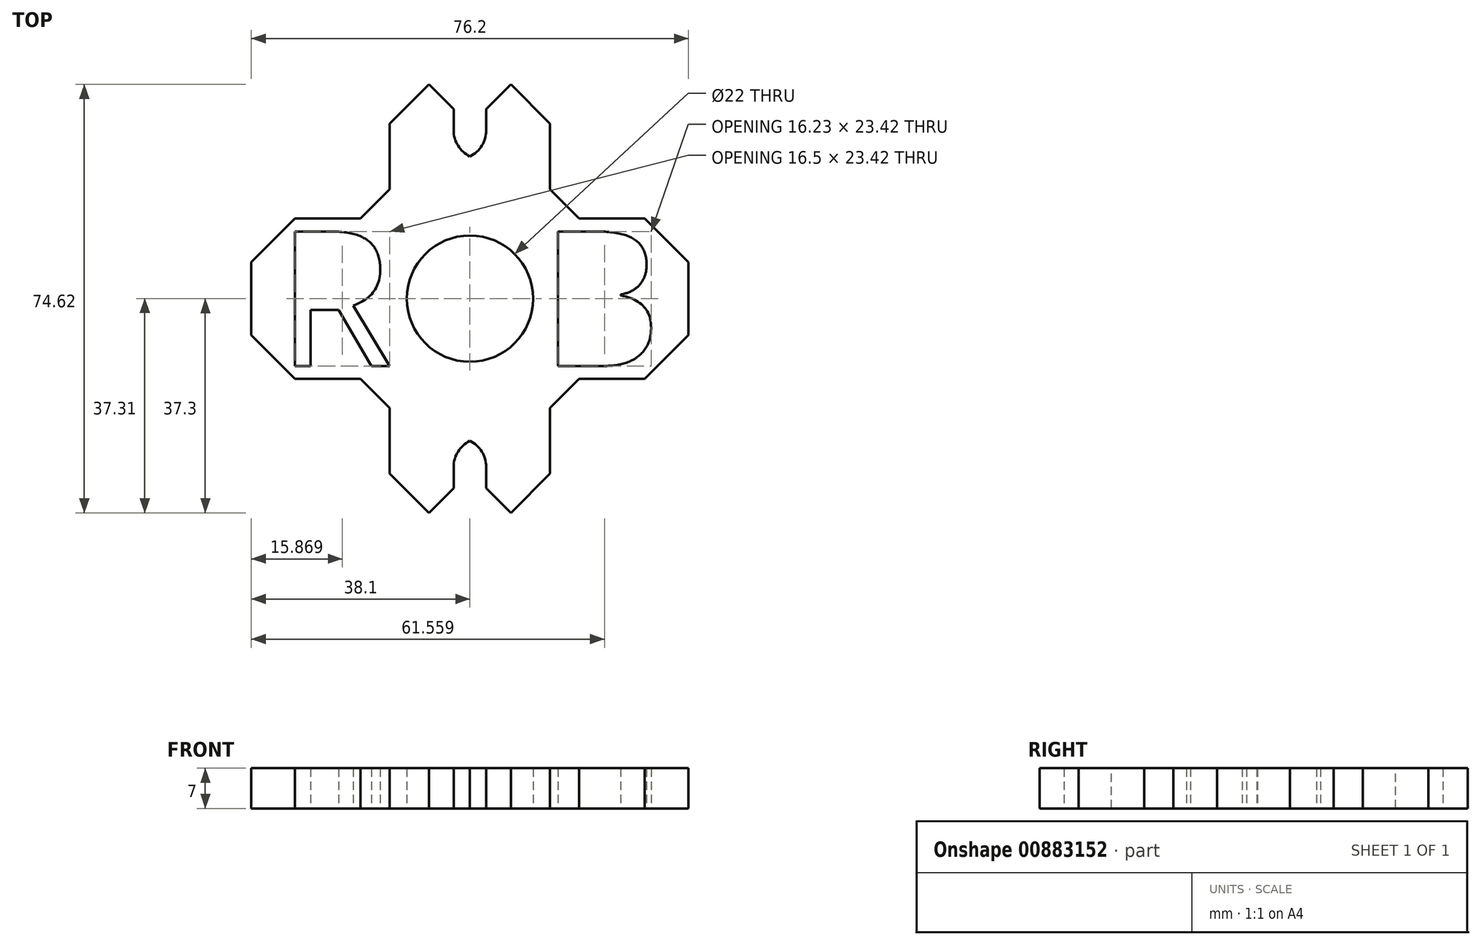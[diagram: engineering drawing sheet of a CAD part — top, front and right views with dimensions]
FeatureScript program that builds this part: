
annotation { "Feature Type Name" : "Feature", "Feature Type Description" : "" }
export const myFeature = defineFeature(function(context is Context, id is Id, definition is map)
    precondition{}
    {
        {
            var Q0;
            Q0=qCreatedBy(makeId("Top.planeOp"),FACE);
            var sketch = newSketch(context, id + "F0", { "sketchPlane" : qUnion([Q0])});
            skCircle(sketch, "E0", {"center": v(0, 0) * mm, "radius": 11 * mm});
            skLineSegment(sketch, "E1.bottom", {"start": v(-38.1, -13.97) * mm, "end": v(38.1, -13.97) * mm});
            skLineSegment(sketch, "E1.top", {"start": v(-38.1, 13.97) * mm, "end": v(38.1, 13.97) * mm});
            skLineSegment(sketch, "E1.left", {"start": v(-38.1, -13.97) * mm, "end": v(-38.1, 13.97) * mm});
            skLineSegment(sketch, "E1.right", {"start": v(38.1, -13.97) * mm, "end": v(38.1, 13.97) * mm});
            skText(sketch, "E2", { "text": "ROB", "fontName": "OpenSans-Regular.ttf"});
            skLineSegment(sketch, "E3.bottom", {"start": v(-13.97, -38.1) * mm, "end": v(13.97, -38.1) * mm});
            skLineSegment(sketch, "E3.top", {"start": v(-13.97, 38.1) * mm, "end": v(13.97, 38.1) * mm});
            skLineSegment(sketch, "E3.left", {"start": v(-13.97, -38.1) * mm, "end": v(-13.97, 38.1) * mm});
            skLineSegment(sketch, "E3.right", {"start": v(13.97, -38.1) * mm, "end": v(13.97, 38.1) * mm});
            const initialGuessF0  = {"E2": [-0.0337, -0.01172, 1, 0, 0.02362]};
            skSetInitialGuess(sketch, initialGuessF0);
            skSolve(sketch);
        }
        {
            var Q0;
            Q0=makeQuery(id+"F0.imprint","IMPRINT",FACE,{"disambiguationData":[TD([[makeQuery(id+"F0.imprint","IMPRINT",EDGE,{"derivedFrom":sQuery(id+"F0.wireOp",EDGE,"E1.bottom")}),1.0]])]});
            var Q1;
            {var subQ0=sQuery(id+"F0.wireOp",EDGE,"E2.sketch_text.stroke-19");Q1=makeQuery(id+"F0.imprint","IMPRINT",FACE,{"disambiguationData":[TD([[makeQuery(id+"F0.imprint","IMPRINT",EDGE,{"derivedFrom":subQ0}),-1.0]])]});}
            extrude(context, id + "F1", {"entities" : qUnion([Q0, Q1]), "depth" : 7 * mm, "offsetDistance" : 25.4 * mm});
        }
        {
            var Q0;
            {var subQ0=sQuery(id+"F0.wireOp",EDGE,"E1.left");Q0=makeQuery(id+"F0.imprint","IMPRINT",FACE,{"disambiguationData":[TD([[makeQuery(id+"F0.imprint","IMPRINT",EDGE,{"derivedFrom":subQ0}),-1.0]])]});}
            var Q1;
            {var subQ6=sQuery(id+"F0.wireOp",EDGE,"E2.sketch_text.stroke-19");Q1=makeQuery(id+"F0.imprint","IMPRINT",FACE,{"disambiguationData":[TD([[makeQuery(id+"F0.imprint","IMPRINT",EDGE,{"derivedFrom":subQ6}),1.0]])]});}
            var Q2;
            {var subQ0=sQuery(id+"F0.wireOp",EDGE,"E2.sketch_text.stroke-19");Q2=makeQuery(id+"F0.imprint","IMPRINT",FACE,{"disambiguationData":[TD([[makeQuery(id+"F0.imprint","IMPRINT",EDGE,{"derivedFrom":subQ0}),-1.0]])]});}
            var Q3;
            {var subQ0=sQuery(id+"F0.wireOp",EDGE,"E1.right");Q3=makeQuery(id+"F0.imprint","IMPRINT",FACE,{"disambiguationData":[TD([[makeQuery(id+"F0.imprint","IMPRINT",EDGE,{"derivedFrom":subQ0}),1.0]])]});}
            var Q4;
            {var subQ5=sQuery(id+"F0.wireOp",EDGE,"E3.top");Q4=makeQuery(id+"F0.imprint","IMPRINT",FACE,{"disambiguationData":[TD([[makeQuery(id+"F0.imprint","IMPRINT",EDGE,{"derivedFrom":subQ5}),-1.0]])]});}
            var Q5;
            {var subQ5=sQuery(id+"F0.wireOp",EDGE,"E3.bottom");Q5=makeQuery(id+"F0.imprint","IMPRINT",FACE,{"disambiguationData":[TD([[makeQuery(id+"F0.imprint","IMPRINT",EDGE,{"derivedFrom":subQ5}),1.0]])]});}
            extrude(context, id + "F2", {"entities" : qUnion([Q0, Q1, Q2, Q3, Q4, Q5]), "operationType" : NewBodyOperationType.ADD, "depth" : 7 * mm, "offsetDistance" : 25.4 * mm});
        }
        {
            var Q0;
            Q0=makeQuery(id+"F2.opExtrude","SWEPT_EDGE",EDGE,{"disambiguationData":[OSD([sQuery(id+"F0.wireOp",EDGE,"E3.top"),sQuery(id+"F0.wireOp",EDGE,"E3.right")])]});
            var Q1;
            Q1=makeQuery(id+"F2.opExtrude","SWEPT_EDGE",EDGE,{"disambiguationData":[OSD([sQuery(id+"F0.wireOp",EDGE,"E3.top"),sQuery(id+"F0.wireOp",EDGE,"E3.left")])]});
            var Q2;
            Q2=makeQuery(id+"F2.opExtrude","SWEPT_EDGE",EDGE,{"disambiguationData":[OSD([sQuery(id+"F0.wireOp",EDGE,"E3.bottom"),sQuery(id+"F0.wireOp",EDGE,"E3.right")])]});
            var Q3;
            Q3=makeQuery(id+"F2.opExtrude","SWEPT_EDGE",EDGE,{"disambiguationData":[OSD([sQuery(id+"F0.wireOp",EDGE,"E3.bottom"),sQuery(id+"F0.wireOp",EDGE,"E3.left")])]});
            var Q4;
            Q4=makeQuery(id+"F2.opExtrude","SWEPT_EDGE",EDGE,{"disambiguationData":[OSD([sQuery(id+"F0.wireOp",EDGE,"E1.bottom"),sQuery(id+"F0.wireOp",EDGE,"E1.right")])]});
            var Q5;
            Q5=makeQuery(id+"F2.opExtrude","SWEPT_EDGE",EDGE,{"disambiguationData":[OSD([sQuery(id+"F0.wireOp",EDGE,"E1.top"),sQuery(id+"F0.wireOp",EDGE,"E1.right")])]});
            var Q6;
            Q6=makeQuery(id+"F2.opExtrude","SWEPT_EDGE",EDGE,{"disambiguationData":[OSD([sQuery(id+"F0.wireOp",EDGE,"E1.bottom"),sQuery(id+"F0.wireOp",EDGE,"E1.left")])]});
            var Q7;
            Q7=makeQuery(id+"F2.opExtrude","SWEPT_EDGE",EDGE,{"disambiguationData":[OSD([sQuery(id+"F0.wireOp",EDGE,"E1.top"),sQuery(id+"F0.wireOp",EDGE,"E1.left")])]});
            chamfer(context, id + "F3", {"entities" : qUnion([Q0, Q1, Q2, Q3, Q4, Q5, Q6, Q7]), "width" : 7.62 * mm, "tangentPropagation" : true});
        }
        {
            var Q0;
            Q0=makeQuery(id+"F2.opExtrude","SWEPT_EDGE",EDGE,{"disambiguationData":[OSD([sQuery(id+"F0.wireOp",EDGE,"E1.bottom"),sQuery(id+"F0.wireOp",EDGE,"E3.left")])]});
            var Q1;
            Q1=makeQuery(id+"F2.opExtrude","SWEPT_EDGE",EDGE,{"disambiguationData":[OSD([sQuery(id+"F0.wireOp",EDGE,"E1.bottom"),sQuery(id+"F0.wireOp",EDGE,"E3.right")])]});
            var Q2;
            Q2=makeQuery(id+"F2.opExtrude","SWEPT_EDGE",EDGE,{"disambiguationData":[OSD([sQuery(id+"F0.wireOp",EDGE,"E1.top"),sQuery(id+"F0.wireOp",EDGE,"E3.left")])]});
            var Q3;
            Q3=makeQuery(id+"F2.opExtrude","SWEPT_EDGE",EDGE,{"disambiguationData":[OSD([sQuery(id+"F0.wireOp",EDGE,"E1.top"),sQuery(id+"F0.wireOp",EDGE,"E3.right")])]});
            chamfer(context, id + "F4", {"entities" : qUnion([Q0, Q1, Q2, Q3]), "width" : 5.08 * mm, "tangentPropagation" : true});
        }
        {
            var Q0;
            Q0=qCreatedBy(makeId("Top.planeOp"),FACE);
            var sketch = newSketch(context, id + "F5", { "sketchPlane" : qUnion([Q0])});
            skLineSegment(sketch, "E4.bottom", {"start": v(-2.85, -24.25) * mm, "end": v(2.85, -24.25) * mm});
            skLineSegment(sketch, "E4.top", {"start": v(-2.85, 24.25) * mm, "end": v(2.85, 24.25) * mm});
            skLineSegment(sketch, "E4.left", {"start": v(-2.85, -24.25) * mm, "end": v(-2.85, 24.25) * mm});
            skLineSegment(sketch, "E4.right", {"start": v(2.85, -24.25) * mm, "end": v(2.85, 24.25) * mm});
            skPoint(sketch, "E4.middle", {"position": v(0, 0) * mm});
            skLineSegment(sketch, "E5.top", {"start": v(-2.85, 51.8) * mm, "end": v(2.85, 51.8) * mm});
            skLineSegment(sketch, "E5.left", {"start": v(-2.85, 24.25) * mm, "end": v(-2.85, 51.8) * mm});
            skLineSegment(sketch, "E5.right", {"start": v(2.85, 24.25) * mm, "end": v(2.85, 51.8) * mm});
            skLineSegment(sketch, "E6.top", {"start": v(-2.85, -44.46) * mm, "end": v(2.85, -44.46) * mm});
            skLineSegment(sketch, "E6.left", {"start": v(-2.85, -24.25) * mm, "end": v(-2.85, -44.46) * mm});
            skLineSegment(sketch, "E6.right", {"start": v(2.85, -24.25) * mm, "end": v(2.85, -44.46) * mm});
            skSolve(sketch);
        }
        {
            var Q0;
            Q0=makeQuery(id+"F5.imprint","IMPRINT",FACE,{"disambiguationData":[TD([[makeQuery(id+"F5.imprint","IMPRINT",EDGE,{"derivedFrom":sQuery(id+"F5.wireOp",EDGE,"E4.top")}),1.0]])]});
            var Q1;
            Q1=makeQuery(id+"F5.imprint","IMPRINT",FACE,{"disambiguationData":[TD([[makeQuery(id+"F5.imprint","IMPRINT",EDGE,{"derivedFrom":sQuery(id+"F5.wireOp",EDGE,"E4.bottom")}),-1.0]])]});
            extrude(context, id + "F6", {"entities" : qUnion([Q0, Q1]), "operationType" : NewBodyOperationType.REMOVE, "depth" : 46.74 * mm, "offsetDistance" : 25.4 * mm});
        }
        {
            var Q0;
            Q0=makeQuery(id+"F6.boolean.opBoolean","INTERSECT",EDGE,{"derivedFrom":[makeQuery(id+"F2.opExtrude","SWEPT_FACE",FACE,{"disambiguationData":[OSD([sQuery(id+"F0.wireOp",EDGE,"E3.top")])]}),makeQuery(id+"F6.opExtrude","SWEPT_FACE",FACE,{"disambiguationData":[OSD([sQuery(id+"F5.wireOp",EDGE,"E5.right")])]})]});
            var Q1;
            Q1=makeQuery(id+"F6.boolean.opBoolean","INTERSECT",EDGE,{"derivedFrom":[makeQuery(id+"F2.opExtrude","SWEPT_FACE",FACE,{"disambiguationData":[OSD([sQuery(id+"F0.wireOp",EDGE,"E3.top")])]}),makeQuery(id+"F6.opExtrude","SWEPT_FACE",FACE,{"disambiguationData":[OSD([sQuery(id+"F5.wireOp",EDGE,"E5.left")])]})]});
            var Q2;
            Q2=makeQuery(id+"F6.boolean.opBoolean","INTERSECT",EDGE,{"derivedFrom":[makeQuery(id+"F2.opExtrude","SWEPT_FACE",FACE,{"disambiguationData":[OSD([sQuery(id+"F0.wireOp",EDGE,"E3.bottom")])]}),makeQuery(id+"F6.opExtrude","SWEPT_FACE",FACE,{"disambiguationData":[OSD([sQuery(id+"F5.wireOp",EDGE,"E6.left")])]})]});
            var Q3;
            Q3=makeQuery(id+"F6.boolean.opBoolean","INTERSECT",EDGE,{"derivedFrom":[makeQuery(id+"F2.opExtrude","SWEPT_FACE",FACE,{"disambiguationData":[OSD([sQuery(id+"F0.wireOp",EDGE,"E3.bottom")])]}),makeQuery(id+"F6.opExtrude","SWEPT_FACE",FACE,{"disambiguationData":[OSD([sQuery(id+"F5.wireOp",EDGE,"E6.right")])]})]});
            chamfer(context, id + "F7", {"entities" : qUnion([Q0, Q1, Q2, Q3]), "width" : 5.08 * mm, "tangentPropagation" : true});
        }
        {
            var Q0;
            Q0=makeQuery(id+"F6.boolean.opBoolean","COPY",EDGE,{"derivedFrom":makeQuery(id+"F6.opExtrude","SWEPT_EDGE",EDGE,{"disambiguationData":[OSD([sQuery(id+"F5.wireOp",EDGE,"E4.right"),sQuery(id+"F5.wireOp",EDGE,"E4.top"),sQuery(id+"F5.wireOp",EDGE,"E5.right")])]})});
            var Q1;
            Q1=makeQuery(id+"F6.boolean.opBoolean","COPY",EDGE,{"derivedFrom":makeQuery(id+"F6.opExtrude","SWEPT_EDGE",EDGE,{"disambiguationData":[OSD([sQuery(id+"F5.wireOp",EDGE,"E4.left"),sQuery(id+"F5.wireOp",EDGE,"E4.top"),sQuery(id+"F5.wireOp",EDGE,"E5.left")])]})});
            var Q2;
            Q2=makeQuery(id+"F6.boolean.opBoolean","COPY",EDGE,{"derivedFrom":makeQuery(id+"F6.opExtrude","SWEPT_EDGE",EDGE,{"disambiguationData":[OSD([sQuery(id+"F5.wireOp",EDGE,"E4.right"),sQuery(id+"F5.wireOp",EDGE,"E4.bottom"),sQuery(id+"F5.wireOp",EDGE,"E6.right")])]})});
            var Q3;
            Q3=makeQuery(id+"F6.boolean.opBoolean","COPY",EDGE,{"derivedFrom":makeQuery(id+"F6.opExtrude","SWEPT_EDGE",EDGE,{"disambiguationData":[OSD([sQuery(id+"F5.wireOp",EDGE,"E4.left"),sQuery(id+"F5.wireOp",EDGE,"E4.bottom"),sQuery(id+"F5.wireOp",EDGE,"E6.left")])]})});
            fillet(context, id + "F8", {"entities" : qUnion([Q0, Q1, Q2, Q3]), "radius" : 5.08 * mm, "tangentPropagation" : true, "allowEdgeOverflow" : false});
        }
    });
